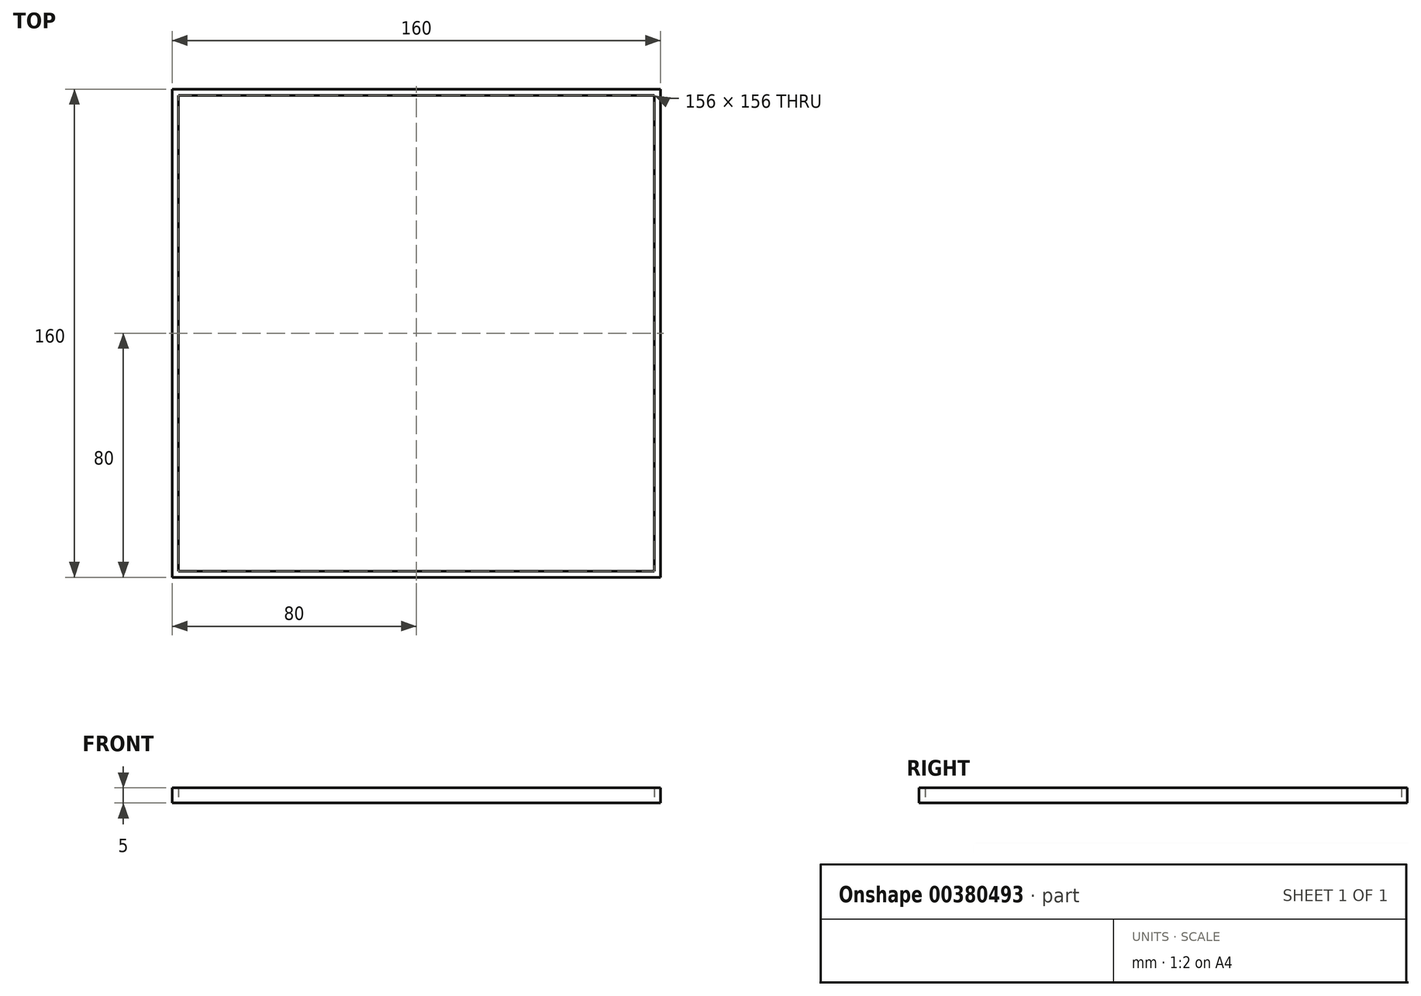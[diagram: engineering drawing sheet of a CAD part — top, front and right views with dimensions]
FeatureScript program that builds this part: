
annotation { "Feature Type Name" : "Feature", "Feature Type Description" : "" }
export const myFeature = defineFeature(function(context is Context, id is Id, definition is map)
    precondition{}
    {
        {
            var Q0;
            Q0=qCreatedBy(makeId("Top.planeOp"),FACE);
            var sketch = newSketch(context, id + "F0", { "sketchPlane" : qUnion([Q0])});
            skLineSegment(sketch, "E0.bottom", {"start": v(-78, -78) * mm, "end": v(78, -78) * mm});
            skLineSegment(sketch, "E0.top", {"start": v(-78, 78) * mm, "end": v(78, 78) * mm});
            skLineSegment(sketch, "E0.left", {"start": v(-78, -78) * mm, "end": v(-78, 78) * mm});
            skLineSegment(sketch, "E0.right", {"start": v(78, -78) * mm, "end": v(78, 78) * mm});
            skPoint(sketch, "E0.middle", {"position": v(0, 0) * mm});
            skLineSegment(sketch, "E1.bottom", {"start": v(-80, -80) * mm, "end": v(80, -80) * mm});
            skLineSegment(sketch, "E1.top", {"start": v(-80, 80) * mm, "end": v(80, 80) * mm});
            skLineSegment(sketch, "E1.left", {"start": v(-80, -80) * mm, "end": v(-80, 80) * mm});
            skLineSegment(sketch, "E1.right", {"start": v(80, -80) * mm, "end": v(80, 80) * mm});
            skSolve(sketch);
        }
        {
            var Q0;
            Q0=makeQuery(id+"F0.imprint","IMPRINT",FACE,{"disambiguationData":[TD([[makeQuery(id+"F0.imprint","IMPRINT",EDGE,{"derivedFrom":sQuery(id+"F0.wireOp",EDGE,"E0.bottom")}),-1.0]])]});
            extrude(context, id + "F1", {"entities" : qUnion([Q0]), "depth" : 5 * mm});
        }
    });
